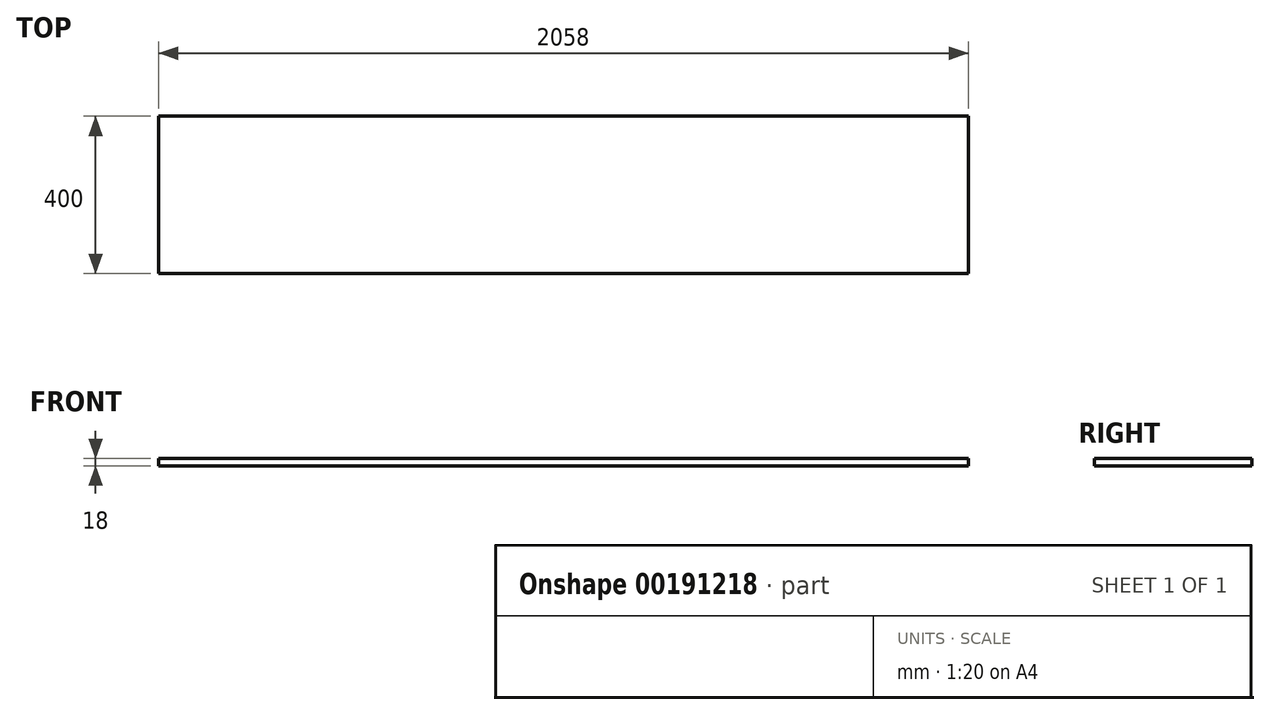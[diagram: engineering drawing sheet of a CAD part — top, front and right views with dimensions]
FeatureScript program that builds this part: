
annotation { "Feature Type Name" : "Feature", "Feature Type Description" : "" }
export const myFeature = defineFeature(function(context is Context, id is Id, definition is map)
    precondition{}
    {
        {
            var Q0;
            Q0=qCreatedBy(makeId("Top.planeOp"),FACE);
            var sketch = newSketch(context, id + "F0", { "sketchPlane" : qUnion([Q0])});
            skLineSegment(sketch, "E0.bottom", {"start": v(0, 0) * mm, "end": v(2058, 0) * mm});
            skLineSegment(sketch, "E0.top", {"start": v(0, 400) * mm, "end": v(2058, 400) * mm});
            skLineSegment(sketch, "E0.left", {"start": v(0, 0) * mm, "end": v(0, 400) * mm});
            skLineSegment(sketch, "E0.right", {"start": v(2058, 0) * mm, "end": v(2058, 400) * mm});
            skSolve(sketch);
        }
        {
            var Q0;
            Q0 = qSketchRegion(id + "F0", true);
            extrude(context, id + "F1", {"entities" : qUnion([Q0]), "depth" : 18 * mm});
        }
    });
